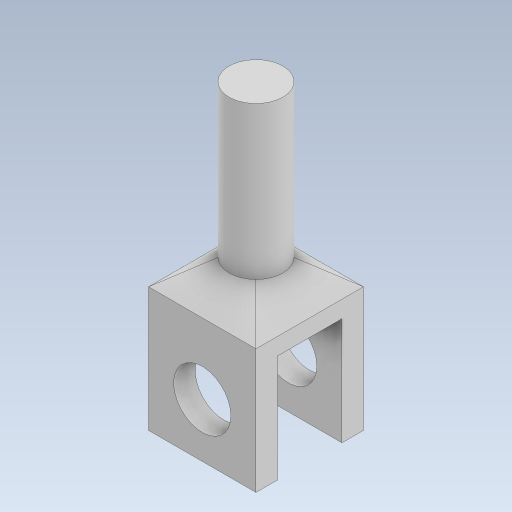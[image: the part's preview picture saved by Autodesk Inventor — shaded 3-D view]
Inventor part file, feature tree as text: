
AUTODESK INVENTOR PART (.ipt)
format: ipt  version: 2023 (Build 270158000, 158)  size: 169,472 bytes
history: native  units: in
note: dims shown in document units (in); Inventor stores cm internally (conversion verified against a paired STEP export)
features: sketch x4, extrude x3, other x2, plane x1, loft x1, hole x1
ambient origin geometry x8: Origin, YZ Plane, XZ Plane, XY Plane, X Axis, Y Axis, Z Axis, Center Point
bodies: Solid1 (feature_tree)
feature tree (12):
  extrude  "Extrusion1"  Depth=0.3in
  plane  "Work Plane1"
  extrude  "Extrusion2"  Depth=0.5in TaperAngle=0.0deg
  extrude  "Extrusion3"  Depth=0.2506in
  loft  "Loft3"
  hole  "Hole1"  [1 undecoded]
  sketch  "Sketch2"  dims[d0=0.1in d1=0.3in]
  sketch  "Sketch3"  dims[d2=0.5in d3=0.5in d4=0.0in]
  sketch  "Sketch4"  dims[d5=0.1969in d6=0.2506in]
  other  "Edges5"
  other  "Edges6"
  sketch  "Sketch7"  dims[d7=0.7087in d8=0.0in d17=0.0787in d18=0.0in d19=0.0in d20=90.0deg d21=0.0in d22=90.0deg d23=0.15in d34=0.266in d35=0.2362in d36=0.507in d37=0.0787in d38=0.5635in d39=0.5in d40=0.8108in]
note: 1 required parameter value undecoded (feature->parameter linkage not recoverable at this tier; creation-order binding heuristic only, values carry confidence <= 0.55)
